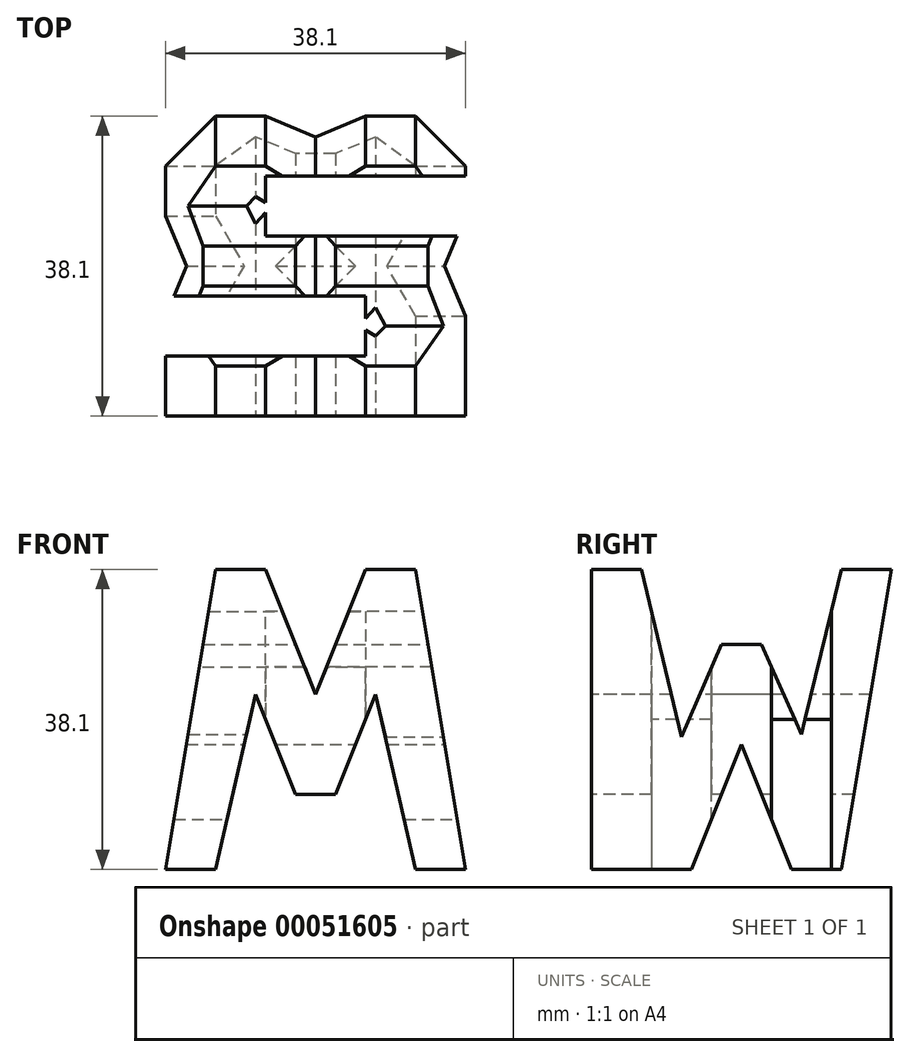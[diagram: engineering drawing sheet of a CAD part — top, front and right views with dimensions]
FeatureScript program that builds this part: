
annotation { "Feature Type Name" : "Feature", "Feature Type Description" : "" }
export const myFeature = defineFeature(function(context is Context, id is Id, definition is map)
    precondition{}
    {
        {
            var Q0;
            Q0=qCreatedBy(makeId("Front.planeOp"),FACE);
            var sketch = newSketch(context, id + "F0", { "sketchPlane" : qUnion([Q0])});
            skLineSegment(sketch, "E0.rect.bottom", {"start": v(0, 38.1) * mm, "end": v(38.1, 38.1) * mm});
            skLineSegment(sketch, "E0.rect.top", {"start": v(0, 0) * mm, "end": v(38.1, 0) * mm});
            skLineSegment(sketch, "E0.rect.left", {"start": v(0, 38.1) * mm, "end": v(0, 0) * mm});
            skLineSegment(sketch, "E0.rect.right", {"start": v(38.1, 38.1) * mm, "end": v(38.1, 0) * mm});
            skSolve(sketch);
        }
        {
            var Q0;
            Q0 = qSketchRegion(id + "F0", true);
            extrude(context, id + "F1", {"entities" : qUnion([Q0]), "depth" : 38.1 * mm});
        }
        {
            var Q0;
            Q0=qCreatedBy(makeId("Front.planeOp"),FACE);
            cPlane(context, id + "F2", {"entities" : qUnion([Q0]), "cplaneType" : CPlaneType.OFFSET, "offset" : 38.1 * mm, "width" : 152.4 * mm, "height" : 152.4 * mm});
        }
        {
            var Q0;
            Q0=qCreatedBy(makeId("Top.planeOp"),FACE);
            cPlane(context, id + "F3", {"entities" : qUnion([Q0]), "cplaneType" : CPlaneType.OFFSET, "offset" : 38.1 * mm, "width" : 152.4 * mm, "height" : 152.4 * mm});
        }
        {
            var Q0;
            Q0=makeQuery(id+"F1.opExtrude","SWEPT_FACE",FACE,{"disambiguationData":[OSD([sQuery(id+"F0.wireOp",EDGE,"E0.rect.right")])]});
            var sketch = newSketch(context, id + "F4", { "sketchPlane" : qUnion([Q0])});
            skLineSegment(sketch, "E1", {"start": v(-38.1, 38.1) * mm, "end": v(-31.75, 0) * mm});
            skLineSegment(sketch, "E2", {"start": v(-31.75, 0) * mm, "end": v(-38.1, 38.1) * mm});
            skLineSegment(sketch, "E3", {"start": v(-31.75, 38.1) * mm, "end": v(-26.67, 16.81) * mm});
            skLineSegment(sketch, "E4", {"start": v(-26.67, 16.81) * mm, "end": v(-21.59, 28.58) * mm});
            skLineSegment(sketch, "E5", {"start": v(-21.59, 28.58) * mm, "end": v(-16.5, 28.58) * mm});
            skLineSegment(sketch, "E6", {"start": v(-16.5, 28.58) * mm, "end": v(-11.43, 17.16) * mm});
            skLineSegment(sketch, "E7", {"start": v(-11.43, 17.16) * mm, "end": v(-6.35, 38.1) * mm});
            skLineSegment(sketch, "E8", {"start": v(0, 38.1) * mm, "end": v(-6.35, 0) * mm});
            skLineSegment(sketch, "E9", {"start": v(-12.7, 0) * mm, "end": v(-19.05, 15.88) * mm});
            skLineSegment(sketch, "E10", {"start": v(-19.05, 15.88) * mm, "end": v(-25.4, 0) * mm});
            skSolve(sketch);
        }
        {
            var Q0;
            {var subQ0=sQuery(id+"F4.wireOp",EDGE,"E3");Q0=makeQuery(id+"F4.imprint","IMPRINT",FACE,{"disambiguationData":[TD([[makeQuery(id+"F4.imprint","IMPRINT",EDGE,{"derivedFrom":subQ0}),1.0]])]});}
            var Q1;
            {var subQ0=sQuery(id+"F4.wireOp",EDGE,"E2");Q1=makeQuery(id+"F4.imprint","IMPRINT",FACE,{"disambiguationData":[TD([[makeQuery(id+"F4.imprint","IMPRINT",EDGE,{"derivedFrom":subQ0}),1.0]])]});}
            var Q2;
            {var subQ0=sQuery(id+"F4.wireOp",EDGE,"E9");Q2=makeQuery(id+"F4.imprint","IMPRINT",FACE,{"disambiguationData":[TD([[makeQuery(id+"F4.imprint","IMPRINT",EDGE,{"derivedFrom":subQ0}),1.0]])]});}
            var Q3;
            {var subQ0=sQuery(id+"F4.wireOp",EDGE,"E8");Q3=makeQuery(id+"F4.imprint","IMPRINT",FACE,{"disambiguationData":[TD([[makeQuery(id+"F4.imprint","IMPRINT",EDGE,{"derivedFrom":subQ0}),1.0]])]});}
            extrude(context, id + "F5", {"entities" : qUnion([Q0, Q1, Q2, Q3]), "operationType" : NewBodyOperationType.REMOVE, "oppositeDirection" : true, "depth" : 38.1 * mm});
        }
        {
            var Q0;
            Q0=qCreatedBy(id+"F2.planeOp",FACE);
            var sketch = newSketch(context, id + "F6", { "sketchPlane" : qUnion([Q0])});
            skLineSegment(sketch, "E11.bottom", {"start": v(0, 0) * mm, "end": v(38.1, 0) * mm});
            skLineSegment(sketch, "E11.top", {"start": v(0, 38.1) * mm, "end": v(38.1, 38.1) * mm});
            skLineSegment(sketch, "E11.left", {"start": v(0, 0) * mm, "end": v(0, 38.1) * mm});
            skLineSegment(sketch, "E11.right", {"start": v(38.1, 0) * mm, "end": v(38.1, 38.1) * mm});
            skLineSegment(sketch, "E12", {"start": v(6.35, 38.1) * mm, "end": v(0, 0) * mm});
            skLineSegment(sketch, "E13", {"start": v(0, 0) * mm, "end": v(6.35, 38.1) * mm});
            skLineSegment(sketch, "E14", {"start": v(12.7, 38.1) * mm, "end": v(19.05, 22.23) * mm});
            skLineSegment(sketch, "E15", {"start": v(19.05, 22.22) * mm, "end": v(25.4, 38.1) * mm});
            skLineSegment(sketch, "E16", {"start": v(31.75, 38.1) * mm, "end": v(38.1, 0) * mm});
            skLineSegment(sketch, "E17", {"start": v(38.1, 0) * mm, "end": v(31.75, 0) * mm});
            skLineSegment(sketch, "E18", {"start": v(31.75, 0) * mm, "end": v(26.67, 22.22) * mm});
            skLineSegment(sketch, "E19", {"start": v(26.67, 22.22) * mm, "end": v(21.6, 9.52) * mm});
            skLineSegment(sketch, "E20", {"start": v(21.6, 9.52) * mm, "end": v(16.51, 9.52) * mm});
            skLineSegment(sketch, "E21", {"start": v(16.51, 9.52) * mm, "end": v(11.43, 22.23) * mm});
            skLineSegment(sketch, "E22", {"start": v(11.43, 22.23) * mm, "end": v(6.35, 0) * mm});
            skSolve(sketch);
        }
        {
            var Q0;
            {var subQ0=sQuery(id+"F6.wireOp",EDGE,"E11.left");Q0=makeQuery(id+"F6.imprint","IMPRINT",FACE,{"disambiguationData":[TD([[makeQuery(id+"F6.imprint","IMPRINT",EDGE,{"derivedFrom":subQ0}),-1.0]])]});}
            var Q1;
            {var subQ0=sQuery(id+"F6.wireOp",EDGE,"E18");Q1=makeQuery(id+"F6.imprint","IMPRINT",FACE,{"disambiguationData":[TD([[makeQuery(id+"F6.imprint","IMPRINT",EDGE,{"derivedFrom":subQ0}),1.0]])]});}
            var Q2;
            {var subQ0=sQuery(id+"F6.wireOp",EDGE,"E14");Q2=makeQuery(id+"F6.imprint","IMPRINT",FACE,{"disambiguationData":[TD([[makeQuery(id+"F6.imprint","IMPRINT",EDGE,{"derivedFrom":subQ0}),1.0]])]});}
            var Q3;
            {var subQ0=sQuery(id+"F6.wireOp",EDGE,"E11.right");Q3=makeQuery(id+"F6.imprint","IMPRINT",FACE,{"disambiguationData":[TD([[makeQuery(id+"F6.imprint","IMPRINT",EDGE,{"derivedFrom":subQ0}),1.0]])]});}
            extrude(context, id + "F7", {"entities" : qUnion([Q0, Q1, Q2, Q3]), "operationType" : NewBodyOperationType.REMOVE, "oppositeDirection" : true, "depth" : 38.1 * mm});
        }
        {
            var Q0;
            Q0=qCreatedBy(id+"F3.planeOp",FACE);
            var sketch = newSketch(context, id + "F8", { "sketchPlane" : qUnion([Q0])});
            skLineSegment(sketch, "E23", {"start": v(0, 0) * mm, "end": v(0, -38.1) * mm});
            skLineSegment(sketch, "E24", {"start": v(0, -38.1) * mm, "end": v(38.1, -38.1) * mm});
            skLineSegment(sketch, "E25", {"start": v(38.1, -38.1) * mm, "end": v(38.1, 0) * mm});
            skLineSegment(sketch, "E26", {"start": v(38.1, 0) * mm, "end": v(0, 0) * mm});
            skLineSegment(sketch, "E27", {"start": v(38.1, -7.62) * mm, "end": v(12.7, -7.62) * mm});
            skLineSegment(sketch, "E28", {"start": v(12.7, -7.62) * mm, "end": v(12.7, -15.24) * mm});
            skLineSegment(sketch, "E29", {"start": v(12.7, -15.24) * mm, "end": v(38.1, -15.24) * mm});
            skLineSegment(sketch, "E30", {"start": v(0, -22.86) * mm, "end": v(25.4, -22.86) * mm});
            skLineSegment(sketch, "E31", {"start": v(25.4, -22.86) * mm, "end": v(25.4, -30.48) * mm});
            skLineSegment(sketch, "E32", {"start": v(25.4, -30.48) * mm, "end": v(0, -30.48) * mm});
            skSolve(sketch);
        }
        {
            var Q0;
            {var subQ0=sQuery(id+"F8.wireOp",EDGE,"E27");Q0=makeQuery(id+"F8.imprint","IMPRINT",FACE,{"disambiguationData":[TD([[makeQuery(id+"F8.imprint","IMPRINT",EDGE,{"derivedFrom":subQ0}),1.0]])]});}
            var Q1;
            {var subQ0=sQuery(id+"F8.wireOp",EDGE,"E30");Q1=makeQuery(id+"F8.imprint","IMPRINT",FACE,{"disambiguationData":[TD([[makeQuery(id+"F8.imprint","IMPRINT",EDGE,{"derivedFrom":subQ0}),-1.0]])]});}
            extrude(context, id + "F9", {"entities" : qUnion([Q0, Q1]), "operationType" : NewBodyOperationType.REMOVE, "oppositeDirection" : true, "depth" : 38.1 * mm});
        }
    });
